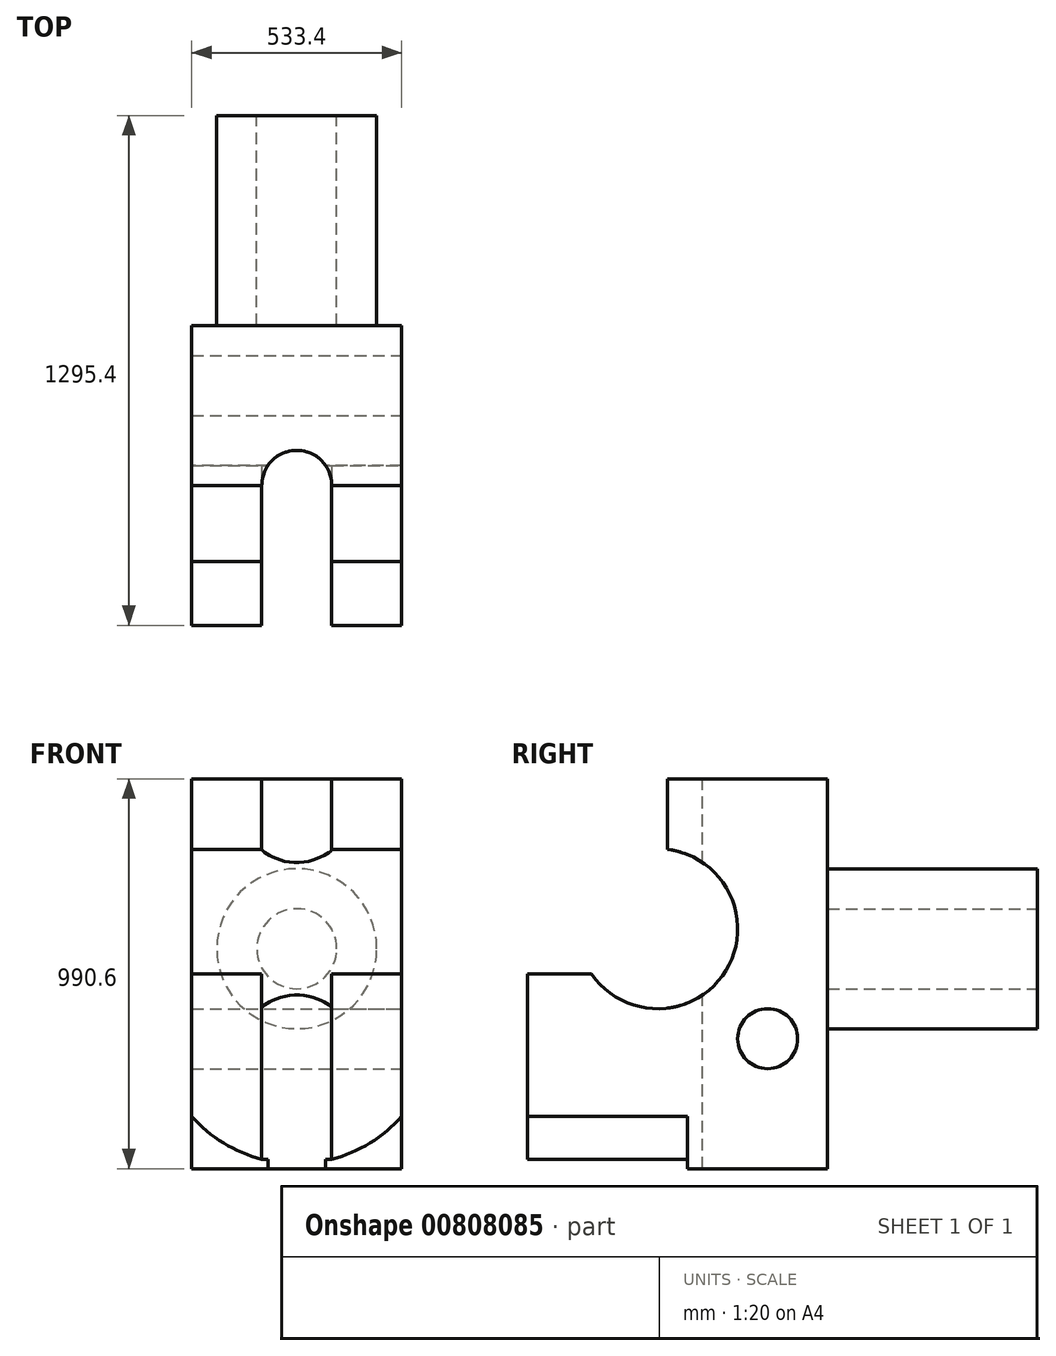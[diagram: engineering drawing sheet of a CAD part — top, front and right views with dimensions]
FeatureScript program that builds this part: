
annotation { "Feature Type Name" : "Feature", "Feature Type Description" : "" }
export const myFeature = defineFeature(function(context is Context, id is Id, definition is map)
    precondition{}
    {
        {
            var Q0;
            Q0=qCreatedBy(makeId("Right.planeOp"),FACE);
            var sketch = newSketch(context, id + "F0", { "sketchPlane" : qUnion([Q0])});
            skLineSegment(sketch, "E0.bottom", {"start": v(381, -495.3) * mm, "end": v(-381, -495.3) * mm});
            skLineSegment(sketch, "E0.top", {"start": v(381, 495.3) * mm, "end": v(-381, 495.3) * mm});
            skLineSegment(sketch, "E0.left", {"start": v(381, -495.3) * mm, "end": v(381, 495.3) * mm});
            skLineSegment(sketch, "E0.right", {"start": v(-381, -495.3) * mm, "end": v(-381, 495.3) * mm});
            skPoint(sketch, "E0.middle", {"position": v(0, 0) * mm});
            skSolve(sketch);
        }
        {
            var Q0;
            Q0 = qSketchRegion(id + "F0", true);
            extrude(context, id + "F1", {"entities" : qUnion([Q0]), "depth" : 533.4 * mm, "offsetDistance" : 25.4 * mm});
        }
        {
            var Q0;
            Q0=makeQuery(id+"F1.opExtrude","SWEPT_FACE",FACE,{"disambiguationData":[OSD([sQuery(id+"F0.wireOp",EDGE,"E0.top")])]});
            var sketch = newSketch(context, id + "F2", { "sketchPlane" : qUnion([Q0])});
            skArc(sketch, "E1", {"start": v(355.6, -25.4) * mm, "mid": v(266.7, 63.5) * mm, "end": v(177.8, -25.4) * mm});
            skPoint(sketch, "E2.start.orphan", {"position": v(266.7, -381) * mm});
            skLineSegment(sketch, "E3", {"start": v(0, -25.4) * mm, "end": v(177.8, -25.4) * mm});
            skLineSegment(sketch, "E4.trimOffspring", {"start": v(355.6, -25.4) * mm, "end": v(533.4, -25.4) * mm});
            skLineSegment(sketch, "E5", {"start": v(177.8, -25.4) * mm, "end": v(177.8, -381) * mm});
            skLineSegment(sketch, "E6", {"start": v(355.6, -25.4) * mm, "end": v(355.6, -381) * mm});
            skSolve(sketch);
        }
        {
            var Q0;
            {var subQ0=sQuery(id+"F2.wireOp",EDGE,"E3");Q0=makeQuery(id+"F2.imprint","IMPRINT",FACE,{"disambiguationData":[TD([[makeQuery(id+"F2.imprint","IMPRINT",EDGE,{"derivedFrom":subQ0}),-1.0]])]});}
            var Q1;
            {var subQ0=sQuery(id+"F2.wireOp",EDGE,"E4.trimOffspring");Q1=makeQuery(id+"F2.imprint","IMPRINT",FACE,{"disambiguationData":[TD([[makeQuery(id+"F2.imprint","IMPRINT",EDGE,{"derivedFrom":subQ0}),-1.0]])]});}
            extrude(context, id + "F3", {"entities" : qUnion([Q0, Q1]), "operationType" : NewBodyOperationType.REMOVE, "oppositeDirection" : true, "depth" : 495.3 * mm, "offsetDistance" : 25.4 * mm});
        }
        {
            var Q0;
            Q0=makeQuery(id+"F2.imprint","IMPRINT",FACE,{"disambiguationData":[TD([[makeQuery(id+"F2.imprint","IMPRINT",EDGE,{"derivedFrom":sQuery(id+"F2.wireOp",EDGE,"E1")}),1.0]])]});
            extrude(context, id + "F4", {"entities" : qUnion([Q0]), "operationType" : NewBodyOperationType.REMOVE, "oppositeDirection" : true, "depth" : 1188.72 * mm, "offsetDistance" : 25.4 * mm});
        }
        {
            var Q0;
            {var subQ1=sQuery(id+"F0.wireOp",EDGE,"E0.right");var subQ3=sQuery(id+"F2.wireOp",EDGE,"E6");Q0=makeQuery(id+"F4.boolean.opBoolean","SPLIT",FACE,{"disambiguationData":[TD([makeQuery(id+"F4.opExtrude","SWEPT_FACE",FACE,{"disambiguationData":[OSD([subQ3])]})])],"derivedFrom":makeQuery(id+"F1.opExtrude","SWEPT_FACE",FACE,{"disambiguationData":[OSD([subQ1])]})});}
            var sketch = newSketch(context, id + "F5", { "sketchPlane" : qUnion([Q0])});
            skLineSegment(sketch, "E7", {"start": v(533.4, 0) * mm, "end": v(266.7, 0) * mm});
            skLineSegment(sketch, "E8", {"start": v(266.7, 0) * mm, "end": v(266.7, -127) * mm});
            skArc(sketch, "E9", {"start": v(0, -362.2) * mm, "mid": v(266.7, -482.6) * mm, "end": v(533.4, -362.2) * mm});
            skSolve(sketch);
        }
        {
            var Q0;
            {var subQ0=sQuery(id+"F5.wireOp",EDGE,"E9");var subQ1=sQuery(id+"F0.wireOp",EDGE,"E0.right");var subQ2=makeQuery(id+"F1.opExtrude","CAP_EDGE",EDGE,{"disambiguationData":[OSD([subQ1])],"isStart":false});var subQ3=makeQuery(id+"F5.imprint","INTERSECT",VERTEX,{"derivedFrom":[subQ2,subQ0]});Q0=makeQuery(id+"F5.imprint","IMPRINT",FACE,{"disambiguationData":[TD([[makeQuery(id+"F5.imprint","IMPRINT",EDGE,{"disambiguationData":[TD([[subQ3,1.0]])],"derivedFrom":subQ0}),-1.0]])]});}
            extrude(context, id + "F6", {"entities" : qUnion([Q0]), "operationType" : NewBodyOperationType.REMOVE, "oppositeDirection" : true, "depth" : 406.4 * mm, "offsetDistance" : 25.4 * mm});
        }
        {
            var Q0;
            {var subQ1=sQuery(id+"F0.wireOp",EDGE,"E0.right");var subQ3=sQuery(id+"F2.wireOp",EDGE,"E5");Q0=makeQuery(id+"F4.boolean.opBoolean","SPLIT",FACE,{"disambiguationData":[TD([makeQuery(id+"F4.opExtrude","SWEPT_FACE",FACE,{"disambiguationData":[OSD([subQ3])]})])],"derivedFrom":makeQuery(id+"F1.opExtrude","SWEPT_FACE",FACE,{"disambiguationData":[OSD([subQ1])]})});}
            var sketch = newSketch(context, id + "F7", { "sketchPlane" : qUnion([Q0])});
            skLineSegment(sketch, "E10", {"start": v(0, 0) * mm, "end": v(266.7, 0) * mm});
            skLineSegment(sketch, "E11", {"start": v(266.7, 0) * mm, "end": v(266.7, -127) * mm});
            skArc(sketch, "E12", {"start": v(0, -362.2) * mm, "mid": v(266.7, -482.6) * mm, "end": v(533.4, -362.2) * mm});
            skSolve(sketch);
        }
        {
            var Q0;
            {var subQ0=sQuery(id+"F7.wireOp",EDGE,"E12");var subQ1=sQuery(id+"F0.wireOp",EDGE,"E0.right");var subQ2=makeQuery(id+"F1.opExtrude","CAP_EDGE",EDGE,{"disambiguationData":[OSD([subQ1])],"isStart":true});var subQ3=makeQuery(id+"F7.imprint","INTERSECT",VERTEX,{"derivedFrom":[subQ2,subQ0]});Q0=makeQuery(id+"F7.imprint","IMPRINT",FACE,{"disambiguationData":[TD([[makeQuery(id+"F7.imprint","IMPRINT",EDGE,{"disambiguationData":[TD([[subQ3,-1.0]])],"derivedFrom":subQ0}),-1.0]])]});}
            extrude(context, id + "F8", {"entities" : qUnion([Q0]), "operationType" : NewBodyOperationType.REMOVE, "oppositeDirection" : true, "depth" : 406.4 * mm, "offsetDistance" : 25.4 * mm});
        }
        {
            var Q0;
            Q0=makeQuery(id+"F1.opExtrude","SWEPT_FACE",FACE,{"disambiguationData":[OSD([sQuery(id+"F0.wireOp",EDGE,"E0.left")])]});
            var sketch = newSketch(context, id + "F9", { "sketchPlane" : qUnion([Q0])});
            skLineSegment(sketch, "E13", {"start": v(-266.7, -495.3) * mm, "end": v(-266.7, 63.5) * mm});
            skCircle(sketch, "E14", {"center": v(-266.7, 63.5) * mm, "radius": 203.2 * mm});
            skSolve(sketch);
        }
        {
            var Q0;
            Q0 = qSketchRegion(id + "F9", true);
            extrude(context, id + "F10", {"entities" : qUnion([Q0]), "operationType" : NewBodyOperationType.ADD, "depth" : 533.4 * mm, "offsetDistance" : 25.4 * mm});
        }
        {
            var Q0;
            Q0=makeQuery(id+"F10.opExtrude","CAP_FACE",FACE,{"disambiguationData":[OSD([sQuery(id+"F9.wireOp",EDGE,"E14")])],"isStart":false});
            var sketch = newSketch(context, id + "F11", { "sketchPlane" : qUnion([Q0])});
            skCircle(sketch, "E15", {"center": v(-266.7, 63.5) * mm, "radius": 101.6 * mm});
            skSolve(sketch);
        }
        {
            var Q0;
            Q0 = qSketchRegion(id + "F11", true);
            extrude(context, id + "F12", {"entities" : qUnion([Q0]), "operationType" : NewBodyOperationType.REMOVE, "oppositeDirection" : true, "depth" : 533.4 * mm, "offsetDistance" : 25.4 * mm});
        }
        {
            var Q0;
            Q0=makeQuery(id+"F8.boolean.opBoolean","COPY",FACE,{"derivedFrom":makeQuery(id+"F8.opExtrude","SWEPT_FACE",FACE,{"disambiguationData":[OSD([sQuery(id+"F0.wireOp",EDGE,"E0.top"),sQuery(id+"F0.wireOp",EDGE,"E0.right"),sQuery(id+"F2.wireOp",EDGE,"E5")])]})});
            var sketch = newSketch(context, id + "F13", { "sketchPlane" : qUnion([Q0])});
            skSolve(sketch);
        }
        {
            var Q0;
            Q0 = qSketchRegion(id + "F13", true);
            var Q1;
            Q1=makeQuery(id+"F6.boolean.opBoolean","COPY",FACE,{"derivedFrom":makeQuery(id+"F6.opExtrude","SWEPT_FACE",FACE,{"disambiguationData":[OSD([sQuery(id+"F0.wireOp",EDGE,"E0.top"),sQuery(id+"F0.wireOp",EDGE,"E0.right"),sQuery(id+"F2.wireOp",EDGE,"E6")])]})});
            extrude(context, id + "F14", {"entities" : qUnion([Q0, Q1]), "operationType" : NewBodyOperationType.REMOVE, "oppositeDirection" : true, "depth" : 751.84 * mm, "offsetDistance" : 25.4 * mm});
        }
        {
            var Q0;
            Q0=makeQuery(id+"F1.opExtrude","CAP_FACE",FACE,{"disambiguationData":[OSD([sQuery(id+"F0.wireOp",EDGE,"E0.bottom"),sQuery(id+"F0.wireOp",EDGE,"E0.top"),sQuery(id+"F0.wireOp",EDGE,"E0.left"),sQuery(id+"F0.wireOp",EDGE,"E0.right")])],"isStart":false});
            var sketch = newSketch(context, id + "F15", { "sketchPlane" : qUnion([Q0])});
            skLineSegment(sketch, "E16", {"start": v(381, -495.3) * mm, "end": v(228.6, -495.3) * mm});
            skLineSegment(sketch, "E17", {"start": v(228.6, -495.3) * mm, "end": v(228.6, -165.1) * mm});
            skCircle(sketch, "E18", {"center": v(228.6, -165.1) * mm, "radius": 76.2 * mm});
            skLineSegment(sketch, "E19", {"start": v(228.6, -165.1) * mm, "end": v(-50.8, -165.1) * mm});
            skLineSegment(sketch, "E20", {"start": v(-50.8, -165.1) * mm, "end": v(-50.8, 114.3) * mm});
            skCircle(sketch, "E21", {"center": v(-50.8, 114.3) * mm, "radius": 203.2 * mm});
            skSolve(sketch);
        }
        {
            var Q0;
            Q0 = qSketchRegion(id + "F15", true);
            extrude(context, id + "F16", {"entities" : qUnion([Q0]), "operationType" : NewBodyOperationType.REMOVE, "oppositeDirection" : true, "depth" : 1084.58 * mm, "offsetDistance" : 25.4 * mm});
        }
    });
